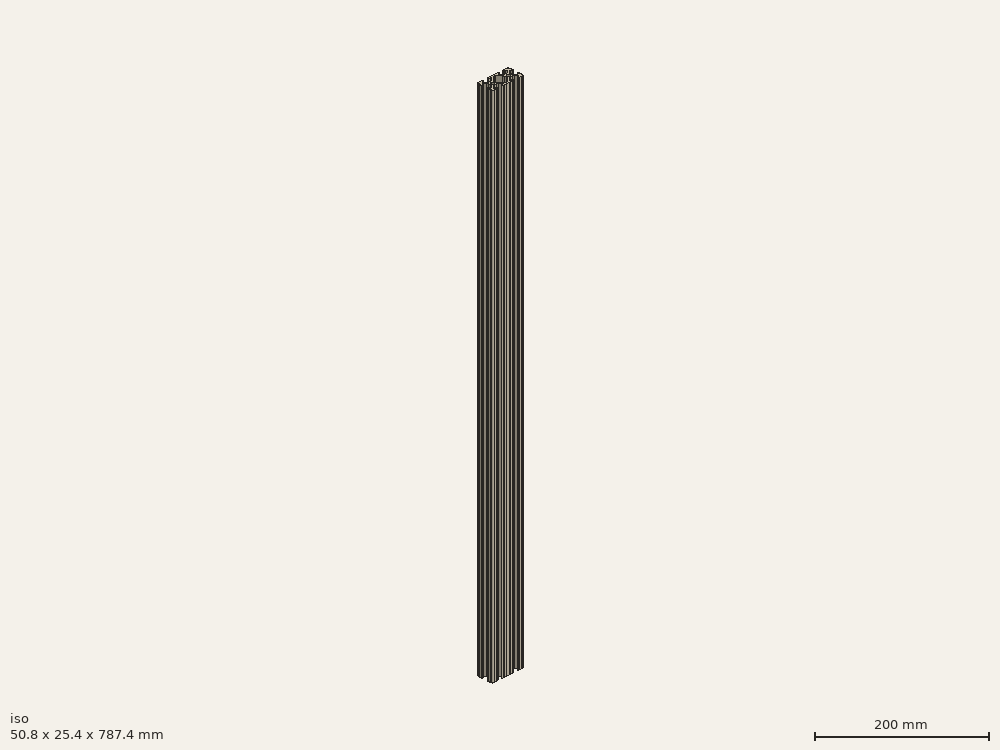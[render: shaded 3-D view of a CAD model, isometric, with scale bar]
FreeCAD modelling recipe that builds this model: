
FCSTD DOCUMENT  (FreeCAD 0.19R24267 (Git))
Label: 1020-31
License: All rights reserved
LicenseURL: http://en.wikipedia.org/wiki/All_rights_reserved
objects: Sketcher::SketchObject×1, Part::Extrusion×1
note: 2 computed .brp shape members not serialized (recipe doc carries the construction recipe); baked Part::Feature solids carry a one-line shape summary decoded from their .brp

FEATURE [Sketcher::SketchObject] Sketch162
  FullyConstrained = false
  sketch-geometry (162):
    g0: LineSegment StartX=7.25951 StartY=3.86941 StartZ=0 EndX=1.54575 EndY=9.57277 EndZ=0
    g1: LineSegment StartX=8.41248 StartY=-10.4902 StartZ=0 EndX=6.28364 EndY=-10.4902 EndZ=0
    g2: ArcOfCircle CenterX=8.41255 CenterY=-11.651 CenterZ=0 NormalX=0 NormalY=0 NormalZ=1 AngleXU=0 Radius=1.04895 StartAngle=4.71239 EndAngle=6.28319
    g3: LineSegment StartX=5.53258 StartY=-8.66607 StartZ=0 EndX=8.80999 EndY=-5.41626 EndZ=0
    g4: LineSegment StartX=9.4615 StartY=-11.651 StartZ=0 EndX=9.4615 EndY=-11.5392 EndZ=0
    g5: ArcOfCircle CenterX=8.41248 CenterY=-11.5392 CenterZ=0 NormalX=0 NormalY=0 NormalZ=1 AngleXU=0 Radius=1.04902 StartAngle=1.15714e-07 EndAngle=1.5708
    g6: ArcOfCircle CenterX=6.28364 CenterY=-9.42351 CenterZ=0 NormalX=0 NormalY=0 NormalZ=1 AngleXU=0 Radius=1.06669 StartAngle=2.35197 EndAngle=4.71239
    g7: LineSegment StartX=-7.28286 StartY=-3.84586 StartZ=0 EndX=-1.67557 EndY=-9.56109 EndZ=0
    g8: LineSegment StartX=1.50403 StartY=-9.57645 StartZ=0 EndX=7.25205 EndY=-3.87684 EndZ=0
    g9: LineSegment StartX=-0.551457 StartY=-10.033 StartZ=0 EndX=0.3952 EndY=-10.033 EndZ=0
    g10: LineSegment StartX=-1.54575 StartY=9.57277 StartZ=0 EndX=-7.25951 EndY=3.86941 EndZ=0
    g11: ArcOfCircle CenterX=0.3952 CenterY=-8.4582 CenterZ=0 NormalX=0 NormalY=0 NormalZ=1 AngleXU=0 Radius=1.5748 StartAngle=4.71239 EndAngle=5.49356
    g12: ArcOfCircle CenterX=5.0165 CenterY=-1.6223 CenterZ=0 NormalX=0 NormalY=0 NormalZ=1 AngleXU=0 Radius=3.175 StartAngle=5.49356 EndAngle=6.28319
    g13: LineSegment StartX=8.1915 StartY=-1.6223 StartZ=0 EndX=8.1915 EndY=1.6223 EndZ=0
    g14: LineSegment StartX=0.433213 StartY=10.033 StartZ=0 EndX=-0.433213 EndY=10.033 EndZ=0
    g15: ArcOfCircle CenterX=-0.551456 CenterY=-8.4582 CenterZ=0 NormalX=0 NormalY=0 NormalZ=1 AngleXU=0 Radius=1.5748 StartAngle=3.91746 EndAngle=4.71239
    g16: ArcOfCircle CenterX=-5.0165 CenterY=1.6223 CenterZ=0 NormalX=0 NormalY=0 NormalZ=1 AngleXU=0 Radius=3.175 StartAngle=2.35528 EndAngle=3.14159
    g17: ArcOfCircle CenterX=-0.433213 CenterY=8.4582 CenterZ=0 NormalX=0 NormalY=0 NormalZ=1 AngleXU=0 Radius=1.5748 StartAngle=1.5708 EndAngle=2.35528
    g18: ArcOfCircle CenterX=5.0165 CenterY=1.6223 CenterZ=0 NormalX=0 NormalY=0 NormalZ=1 AngleXU=0 Radius=3.175 StartAngle=2.15656e-07 EndAngle=0.78631
    g19: Circle CenterX=12.7 CenterY=-2.5e-15 CenterZ=0 NormalX=0 NormalY=0 NormalZ=-1 AngleXU=0 Radius=2.6035
    g20: Circle CenterX=-12.7 CenterY=2.5e-15 CenterZ=0 NormalX=0 NormalY=0 NormalZ=-1 AngleXU=0 Radius=2.6035
    g21: LineSegment StartX=-8.1915 StartY=1.6223 StartZ=0 EndX=-8.1915 EndY=-1.6223 EndZ=0
    g22: LineSegment StartX=-2.13358 StartY=-12.7 StartZ=0 EndX=2.13358 EndY=-12.7 EndZ=0
    g23: ArcOfCircle CenterX=-5.0165 CenterY=-1.6223 CenterZ=0 NormalX=0 NormalY=0 NormalZ=1 AngleXU=0 Radius=3.175 StartAngle=3.14159 EndAngle=3.91746
    g24: LineSegment StartX=3.14958 StartY=-12.7 StartZ=0 EndX=6.3669 EndY=-12.7 EndZ=0
    g25: ArcOfCircle CenterX=6.8749 CenterY=-12.7 CenterZ=0 NormalX=0 NormalY=0 NormalZ=1 AngleXU=0 Radius=0.508 StartAngle=0 EndAngle=3.14159
    g26: LineSegment StartX=-6.28939 StartY=-10.4902 StartZ=0 EndX=-8.41248 EndY=-10.4902 EndZ=0
    g27: LineSegment StartX=-8.41255 StartY=-12.7 StartZ=0 EndX=-7.38288 EndY=-12.7 EndZ=0
    g28: ArcOfCircle CenterX=0.433213 CenterY=8.4582 CenterZ=0 NormalX=0 NormalY=0 NormalZ=1 AngleXU=0 Radius=1.5748 StartAngle=0.78631 EndAngle=1.5708
    g29: ArcOfCircle CenterX=2.64158 CenterY=-12.7 CenterZ=0 NormalX=0 NormalY=0 NormalZ=1 AngleXU=0 Radius=0.508 StartAngle=0 EndAngle=3.14159
    g30: ArcOfCircle CenterX=-16.9875 CenterY=-11.5392 CenterZ=0 NormalX=0 NormalY=0 NormalZ=1 AngleXU=0 Radius=1.04902 StartAngle=1.16223e-07 EndAngle=1.5708
    g31: LineSegment StartX=-8.81696 StartY=-5.44724 StartZ=0 EndX=-5.56415 EndY=-8.76265 EndZ=0
    g32: LineSegment StartX=-16.9875 StartY=-10.4902 StartZ=0 EndX=-19.1164 EndY=-10.4902 EndZ=0
    g33: ArcOfCircle CenterX=-11.0833 CenterY=-7.6708 CenterZ=0 NormalX=0 NormalY=0 NormalZ=1 AngleXU=0 Radius=3.175 StartAngle=0.775866 EndAngle=1.5708
    g34: ArcOfCircle CenterX=-14.3449 CenterY=-7.6708 CenterZ=0 NormalX=0 NormalY=0 NormalZ=1 AngleXU=0 Radius=3.175 StartAngle=1.5708 EndAngle=2.3692
    g35: ArcOfCircle CenterX=-19.1164 CenterY=-9.4742 CenterZ=0 NormalX=0 NormalY=0 NormalZ=1 AngleXU=0 Radius=1.016 StartAngle=2.3692 EndAngle=4.71239
    g36: ArcOfCircle CenterX=-8.41248 CenterY=-11.5392 CenterZ=0 NormalX=0 NormalY=0 NormalZ=1 AngleXU=0 Radius=1.04902 StartAngle=1.5708 EndAngle=3.14159
    g37: LineSegment StartX=7.3829 StartY=-12.7 StartZ=0 EndX=8.41255 EndY=-12.7 EndZ=0
    g38: ArcOfCircle CenterX=-8.41255 CenterY=-11.651 CenterZ=0 NormalX=0 NormalY=0 NormalZ=1 AngleXU=0 Radius=1.04895 StartAngle=3.14159 EndAngle=4.71239
    g39: ArcOfCircle CenterX=14.3545 CenterY=-7.6708 CenterZ=0 NormalX=0 NormalY=0 NormalZ=1 AngleXU=0 Radius=3.175 StartAngle=0.789627 EndAngle=1.5708
    g40: ArcOfCircle CenterX=20.3835 CenterY=-1.55362 CenterZ=0 NormalX=0 NormalY=0 NormalZ=1 AngleXU=0 Radius=3.175 StartAngle=3.14159 EndAngle=3.93122
    g41: LineSegment StartX=23.1902 StartY=6.498 StartZ=0 EndX=23.1902 EndY=4.28752 EndZ=0
    g42: LineSegment StartX=-14.3449 StartY=-4.4958 StartZ=0 EndX=-11.0833 EndY=-4.4958 EndZ=0
    g43: LineSegment StartX=-19.8441 StartY=-8.76517 StartZ=0 EndX=-16.619 EndY=-5.45511 EndZ=0
    g44: LineSegment StartX=-6.36688 StartY=-12.7 StartZ=0 EndX=-3.14958 EndY=-12.7 EndZ=0
    g45: ArcOfCircle CenterX=-6.28939 CenterY=-9.4742 CenterZ=0 NormalX=0 NormalY=0 NormalZ=1 AngleXU=0 Radius=1.016 StartAngle=4.71239 EndAngle=7.05905
    g46: LineSegment StartX=-9.4615 StartY=-11.5392 StartZ=0 EndX=-9.4615 EndY=-11.6511 EndZ=0
    g47: ArcOfCircle CenterX=-6.87488 CenterY=-12.7 CenterZ=0 NormalX=0 NormalY=0 NormalZ=1 AngleXU=0 Radius=0.508 StartAngle=0 EndAngle=3.14159
    g48: LineSegment StartX=-15.9385 StartY=-11.651 StartZ=0 EndX=-15.9385 EndY=-11.5392 EndZ=0
    g49: ArcOfCircle CenterX=-2.64158 CenterY=-12.7 CenterZ=0 NormalX=0 NormalY=0 NormalZ=1 AngleXU=0 Radius=0.508 StartAngle=0 EndAngle=3.14159
    g50: ArcOfCircle CenterX=22.1596 CenterY=-6.33474 CenterZ=0 NormalX=0 NormalY=0 NormalZ=1 AngleXU=0 Radius=1.03057 StartAngle=3.93122 EndAngle=6.28319
    g51: ArcOfCircle CenterX=25.4 CenterY=5.82513 CenterZ=0 NormalX=0 NormalY=0 NormalZ=1 AngleXU=0 Radius=0.508 StartAngle=1.5708 EndAngle=4.71239
    g52: LineSegment StartX=25.4 StartY=6.33313 StartZ=0 EndX=25.4 EndY=9.5504 EndZ=0
    g53: LineSegment StartX=19.0331 StartY=-12.7 StartZ=0 EndX=22.2504 EndY=-12.7 EndZ=0
    g54: ArcOfCircle CenterX=20.3835 CenterY=1.69518 CenterZ=0 NormalX=0 NormalY=0 NormalZ=1 AngleXU=0 Radius=3.175 StartAngle=2.35528 EndAngle=3.14159
    g55: LineSegment StartX=16.9875 StartY=-12.7 StartZ=0 EndX=18.0171 EndY=-12.7 EndZ=0
    g56: ArcOfCircle CenterX=23.2918 CenterY=10.5918 CenterZ=0 NormalX=0 NormalY=0 NormalZ=1 AngleXU=0 Radius=2.1082 StartAngle=6.27114 EndAngle=7.86603
    g57: ArcOfCircle CenterX=24.2392 CenterY=-4.28752 CenterZ=0 NormalX=0 NormalY=0 NormalZ=1 AngleXU=0 Radius=1.04902 StartAngle=1.5708 EndAngle=3.14159
    g58: ArcOfCircle CenterX=24.401 CenterY=-4.23752 CenterZ=0 NormalX=0 NormalY=0 NormalZ=1 AngleXU=0 Radius=0.99902 StartAngle=1.41033e-07 EndAngle=1.5708
    g59: LineSegment StartX=16.59 StartY=-5.41626 StartZ=0 EndX=19.8674 EndY=-8.66607 EndZ=0
    g60: ArcOfCircle CenterX=16.9875 CenterY=-11.5392 CenterZ=0 NormalX=0 NormalY=0 NormalZ=1 AngleXU=0 Radius=1.04902 StartAngle=1.5708 EndAngle=3.14159
    g61: LineSegment StartX=22.2504 StartY=12.7 StartZ=0 EndX=19.0331 EndY=12.7 EndZ=0
    g62: ArcOfCircle CenterX=23.2918 CenterY=-10.5918 CenterZ=0 NormalX=0 NormalY=0 NormalZ=1 AngleXU=0 Radius=2.1082 StartAngle=4.70034 EndAngle=6.29523
    g63: ArcOfCircle CenterX=11.0455 CenterY=-7.6708 CenterZ=0 NormalX=0 NormalY=0 NormalZ=1 AngleXU=0 Radius=3.175 StartAngle=1.5708 EndAngle=2.35197
    g64: ArcOfCircle CenterX=22.7584 CenterY=12.7 CenterZ=0 NormalX=0 NormalY=0 NormalZ=1 AngleXU=0 Radius=0.508 StartAngle=3.14159 EndAngle=6.28288
    g65: LineSegment StartX=19.1164 StartY=-10.4902 StartZ=0 EndX=16.9875 EndY=-10.4902 EndZ=0
    g66: ArcOfCircle CenterX=22.7584 CenterY=-12.7 CenterZ=0 NormalX=0 NormalY=0 NormalZ=1 AngleXU=0 Radius=0.508 StartAngle=0.000301216 EndAngle=3.14159
    g67: ArcOfCircle CenterX=16.9875 CenterY=11.651 CenterZ=0 NormalX=0 NormalY=0 NormalZ=1 AngleXU=0 Radius=1.04902 StartAngle=1.5708 EndAngle=3.14159
    g68: ArcOfCircle CenterX=24.351 CenterY=4.28752 CenterZ=0 NormalX=0 NormalY=0 NormalZ=1 AngleXU=0 Radius=1.04902 StartAngle=4.71239 EndAngle=6.28319
    g69: ArcOfCircle CenterX=19.1164 CenterY=9.4742 CenterZ=0 NormalX=0 NormalY=0 NormalZ=1 AngleXU=0 Radius=1.016 StartAngle=5.49688 EndAngle=7.85398
    g70: LineSegment StartX=19.8341 StartY=8.75512 StartZ=0 EndX=16.4966 EndY=5.42369 EndZ=0
    g71: LineSegment StartX=18.0171 StartY=12.7 StartZ=0 EndX=16.9875 EndY=12.7 EndZ=0
    g72: ArcOfCircle CenterX=18.5251 CenterY=-12.7 CenterZ=0 NormalX=0 NormalY=0 NormalZ=1 AngleXU=0 Radius=0.508 StartAngle=0 EndAngle=3.14159
    g73: LineSegment StartX=15.9384 StartY=11.651 StartZ=0 EndX=15.9384 EndY=11.5392 EndZ=0
    g74: LineSegment StartX=16.9875 StartY=10.4902 StartZ=0 EndX=19.1164 EndY=10.4902 EndZ=0
    g75: LineSegment StartX=11.0455 StartY=-4.4958 StartZ=0 EndX=14.3545 EndY=-4.4958 EndZ=0
    g76: ArcOfCircle CenterX=14.2536 CenterY=7.6708 CenterZ=0 NormalX=0 NormalY=0 NormalZ=1 AngleXU=0 Radius=3.175 StartAngle=4.71239 EndAngle=5.49688
    g77: ArcOfCircle CenterX=25.4 CenterY=-5.82508 CenterZ=0 NormalX=0 NormalY=0 NormalZ=1 AngleXU=0 Radius=0.508 StartAngle=1.5708 EndAngle=4.71239
    g78: LineSegment StartX=18.1405 StartY=3.94229 StartZ=0 EndX=21.4316 EndY=7.22739 EndZ=0
    g79: LineSegment StartX=25.4 StartY=-5.31708 StartZ=0 EndX=25.4 EndY=-4.23752 EndZ=0
    g80: LineSegment StartX=14.2536 StartY=4.4958 StartZ=0 EndX=11.1464 EndY=4.4958 EndZ=0
    g81: ArcOfCircle CenterX=18.5251 CenterY=12.7 CenterZ=0 NormalX=0 NormalY=0 NormalZ=1 AngleXU=0 Radius=0.508 StartAngle=3.14159 EndAngle=6.28319
    g82: LineSegment StartX=23.1902 StartY=-4.28752 StartZ=0 EndX=23.1902 EndY=-6.33474 EndZ=0
    g83: LineSegment StartX=24.401 StartY=-3.2385 StartZ=0 EndX=24.2392 EndY=-3.2385 EndZ=0
    g84: ArcOfCircle CenterX=22.1596 CenterY=6.498 CenterZ=0 NormalX=0 NormalY=0 NormalZ=1 AngleXU=0 Radius=1.03057 StartAngle=0 EndAngle=2.35528
    g85: LineSegment StartX=15.9385 StartY=-11.5392 StartZ=0 EndX=15.9385 EndY=-11.6511 EndZ=0
    g86: LineSegment StartX=25.4 StartY=4.28752 StartZ=0 EndX=25.4 EndY=5.31713 EndZ=0
    g87: ArcOfCircle CenterX=11.1464 CenterY=7.6708 CenterZ=0 NormalX=0 NormalY=0 NormalZ=1 AngleXU=0 Radius=3.175 StartAngle=3.9279 EndAngle=4.71239
    g88: LineSegment StartX=8.90339 StartY=5.42369 StartZ=0 EndX=5.56588 EndY=8.75512 EndZ=0
    g89: LineSegment StartX=21.434 StartY=-7.06654 StartZ=0 EndX=18.148 EndY=-3.80816 EndZ=0
    g90: ArcOfCircle CenterX=25.4 CenterY=10.0584 CenterZ=0 NormalX=0 NormalY=0 NormalZ=1 AngleXU=0 Radius=0.508 StartAngle=1.5711 EndAngle=4.71239
    g91: ArcOfCircle CenterX=16.9875 CenterY=-11.651 CenterZ=0 NormalX=0 NormalY=0 NormalZ=1 AngleXU=0 Radius=1.04895 StartAngle=3.14159 EndAngle=4.71239
    g92: ArcOfCircle CenterX=19.1164 CenterY=-9.42352 CenterZ=0 NormalX=0 NormalY=0 NormalZ=1 AngleXU=0 Radius=1.06668 StartAngle=4.71239 EndAngle=7.07281
    g93: ArcOfCircle CenterX=24.2392 CenterY=4.28752 CenterZ=0 NormalX=0 NormalY=0 NormalZ=1 AngleXU=0 Radius=1.04902 StartAngle=3.14159 EndAngle=4.71239
    g94: ArcOfCircle CenterX=16.9875 CenterY=11.5392 CenterZ=0 NormalX=0 NormalY=0 NormalZ=1 AngleXU=0 Radius=1.04902 StartAngle=3.14159 EndAngle=4.71239
    g95: ArcOfCircle CenterX=25.4 CenterY=-10.0584 CenterZ=0 NormalX=0 NormalY=0 NormalZ=1 AngleXU=0 Radius=0.508 StartAngle=1.5708 EndAngle=4.71209
    g96: ArcOfCircle CenterX=6.87487 CenterY=12.7 CenterZ=0 NormalX=0 NormalY=0 NormalZ=1 AngleXU=0 Radius=0.508 StartAngle=3.14159 EndAngle=6.28319
    g97: LineSegment StartX=25.4 StartY=-9.5504 StartZ=0 EndX=25.4 EndY=-6.33308 EndZ=0
    g98: LineSegment StartX=17.2085 StartY=-1.55362 StartZ=0 EndX=17.2085 EndY=1.69518 EndZ=0
    g99: LineSegment StartX=-9.46155 StartY=11.651 StartZ=0 EndX=-9.46155 EndY=11.5392 EndZ=0
    g100: LineSegment StartX=24.2392 StartY=3.2385 StartZ=0 EndX=24.351 EndY=3.2385 EndZ=0
    g101: LineSegment StartX=-8.41253 StartY=10.4902 StartZ=0 EndX=-6.28939 EndY=10.4902 EndZ=0
    g102: ArcOfCircle CenterX=-10.8409 CenterY=7.6708 CenterZ=0 NormalX=0 NormalY=0 NormalZ=1 AngleXU=0 Radius=3.175 StartAngle=4.71239 EndAngle=5.49688
    g103: LineSegment StartX=-19.1164 StartY=10.4902 StartZ=0 EndX=-16.9875 EndY=10.4902 EndZ=0
    g104: LineSegment StartX=-10.8409 StartY=4.4958 StartZ=0 EndX=-14.1026 EndY=4.4958 EndZ=0
    g105: LineSegment StartX=-16.1879 StartY=5.27664 StartZ=0 EndX=-19.8682 EndY=8.48225 EndZ=0
    g106: LineSegment StartX=-7.38291 StartY=12.7 StartZ=0 EndX=-8.41253 EndY=12.7 EndZ=0
    g107: ArcOfCircle CenterX=-6.28939 CenterY=9.34546 CenterZ=0 NormalX=0 NormalY=0 NormalZ=1 AngleXU=0 Radius=1.14474 StartAngle=5.49688 EndAngle=7.85398
    g108: LineSegment StartX=6.28364 StartY=10.4902 StartZ=0 EndX=8.41253 EndY=10.4902 EndZ=0
    g109: ArcOfCircle CenterX=8.41253 CenterY=11.651 CenterZ=0 NormalX=0 NormalY=0 NormalZ=1 AngleXU=0 Radius=1.04902 StartAngle=4.29175e-07 EndAngle=1.5708
    g110: LineSegment StartX=9.46155 StartY=11.5392 StartZ=0 EndX=9.46155 EndY=11.651 EndZ=0
    g111: ArcOfCircle CenterX=-14.1026 CenterY=7.6708 CenterZ=0 NormalX=0 NormalY=0 NormalZ=1 AngleXU=0 Radius=3.175 StartAngle=3.99583 EndAngle=4.71239
    g112: LineSegment StartX=-5.48068 StartY=8.53527 StartZ=0 EndX=-8.59793 EndY=5.42369 EndZ=0
    g113: ArcOfCircle CenterX=-19.1164 CenterY=9.34546 CenterZ=0 NormalX=0 NormalY=0 NormalZ=1 AngleXU=0 Radius=1.14474 StartAngle=1.5708 EndAngle=3.99583
    g114: LineSegment StartX=8.41253 StartY=12.7 StartZ=0 EndX=7.38287 EndY=12.7 EndZ=0
    g115: LineSegment StartX=-3.14958 StartY=12.7 StartZ=0 EndX=-6.36691 EndY=12.7 EndZ=0
    g116: ArcOfCircle CenterX=-8.41253 CenterY=11.5392 CenterZ=0 NormalX=0 NormalY=0 NormalZ=1 AngleXU=0 Radius=1.04902 StartAngle=3.14159 EndAngle=4.71239
    g117: ArcOfCircle CenterX=8.41253 CenterY=11.5392 CenterZ=0 NormalX=0 NormalY=0 NormalZ=1 AngleXU=0 Radius=1.04902 StartAngle=4.71239 EndAngle=6.28319
    g118: ArcOfCircle CenterX=-6.87491 CenterY=12.7 CenterZ=0 NormalX=0 NormalY=0 NormalZ=1 AngleXU=0 Radius=0.508 StartAngle=3.14159 EndAngle=6.28319
    g119: ArcOfCircle CenterX=-8.41253 CenterY=11.651 CenterZ=0 NormalX=0 NormalY=0 NormalZ=1 AngleXU=0 Radius=1.04902 StartAngle=1.5708 EndAngle=3.14159
    g120: ArcOfCircle CenterX=-2.64159 CenterY=12.7 CenterZ=0 NormalX=0 NormalY=0 NormalZ=1 AngleXU=0 Radius=0.507987 StartAngle=3.14159 EndAngle=6.28319
    g121: ArcOfCircle CenterX=6.28364 CenterY=9.4742 CenterZ=0 NormalX=0 NormalY=0 NormalZ=1 AngleXU=0 Radius=1.016 StartAngle=1.5708 EndAngle=3.9279
    g122: LineSegment StartX=2.13361 StartY=12.7 StartZ=0 EndX=-2.13361 EndY=12.7 EndZ=0
    g123: LineSegment StartX=6.36687 StartY=12.7 StartZ=0 EndX=3.14961 EndY=12.7 EndZ=0
    g124: ArcOfCircle CenterX=-24.401 CenterY=4.23752 CenterZ=0 NormalX=0 NormalY=0 NormalZ=1 AngleXU=0 Radius=0.99902 StartAngle=3.14159 EndAngle=4.71239
    g125: LineSegment StartX=-16.9875 StartY=12.7 StartZ=0 EndX=-18.0171 EndY=12.7 EndZ=0
    g126: LineSegment StartX=-24.401 StartY=3.2385 StartZ=0 EndX=-24.1892 EndY=3.2385 EndZ=0
    g127: ArcOfCircle CenterX=2.64161 CenterY=12.7 CenterZ=0 NormalX=0 NormalY=0 NormalZ=1 AngleXU=0 Radius=0.508 StartAngle=3.14159 EndAngle=6.28319
    g128: ArcOfCircle CenterX=-22.2207 CenterY=-6.67687 CenterZ=0 NormalX=0 NormalY=0 NormalZ=1 AngleXU=0 Radius=0.969476 StartAngle=3.14159 EndAngle=5.51079
    g129: LineSegment StartX=-18.1094 StartY=-3.8465 StartZ=0 EndX=-21.5263 EndY=-7.35342 EndZ=0
    g130: LineSegment StartX=-17.2085 StartY=1.63081 StartZ=0 EndX=-17.2085 EndY=-1.63081 EndZ=0
    g131: ArcOfCircle CenterX=-22.2207 CenterY=6.15588 CenterZ=0 NormalX=0 NormalY=0 NormalZ=1 AngleXU=0 Radius=0.969476 StartAngle=0.854233 EndAngle=3.14159
    g132: LineSegment StartX=-24.1892 StartY=-3.2385 StartZ=0 EndX=-24.401 EndY=-3.2385 EndZ=0
    g133: ArcOfCircle CenterX=-25.4 CenterY=10.0584 CenterZ=0 NormalX=0 NormalY=0 NormalZ=1 AngleXU=0 Radius=0.508 StartAngle=4.71239 EndAngle=7.85368
    g134: LineSegment StartX=-23.1902 StartY=-6.67687 StartZ=0 EndX=-23.1902 EndY=-4.23752 EndZ=0
    g135: ArcOfCircle CenterX=-20.3835 CenterY=-1.63081 CenterZ=0 NormalX=0 NormalY=0 NormalZ=1 AngleXU=0 Radius=3.175 StartAngle=5.51079 EndAngle=6.28319
    g136: ArcOfCircle CenterX=-24.1892 CenterY=-4.23752 CenterZ=0 NormalX=0 NormalY=0 NormalZ=1 AngleXU=0 Radius=0.99902 StartAngle=1.41033e-07 EndAngle=1.5708
    g137: ArcOfCircle CenterX=-25.4 CenterY=5.82508 CenterZ=0 NormalX=0 NormalY=0 NormalZ=1 AngleXU=0 Radius=0.508 StartAngle=4.71239 EndAngle=7.85398
    g138: LineSegment StartX=-23.1902 StartY=4.23752 StartZ=0 EndX=-23.1902 EndY=6.15588 EndZ=0
    g139: LineSegment StartX=-15.9384 StartY=11.5392 StartZ=0 EndX=-15.9384 EndY=11.651 EndZ=0
    g140: ArcOfCircle CenterX=-22.7584 CenterY=12.7 CenterZ=0 NormalX=0 NormalY=0 NormalZ=1 AngleXU=0 Radius=0.508 StartAngle=3.14189 EndAngle=6.28319
    g141: LineSegment StartX=-19.0331 StartY=12.7 StartZ=0 EndX=-22.2504 EndY=12.7 EndZ=0
    g142: ArcOfCircle CenterX=-16.9875 CenterY=11.651 CenterZ=0 NormalX=0 NormalY=0 NormalZ=1 AngleXU=0 Radius=1.04902 StartAngle=4.28571e-07 EndAngle=1.5708
    g143: ArcOfCircle CenterX=-18.5251 CenterY=12.7 CenterZ=0 NormalX=0 NormalY=0 NormalZ=1 AngleXU=0 Radius=0.508 StartAngle=3.14159 EndAngle=6.28319
    g144: ArcOfCircle CenterX=-24.1892 CenterY=4.23752 CenterZ=0 NormalX=0 NormalY=0 NormalZ=1 AngleXU=0 Radius=0.99902 StartAngle=4.71239 EndAngle=6.28319
    g145: LineSegment StartX=-25.4 StartY=5.31708 StartZ=0 EndX=-25.4 EndY=4.23752 EndZ=0
    g146: ArcOfCircle CenterX=-16.9875 CenterY=11.5392 CenterZ=0 NormalX=0 NormalY=0 NormalZ=1 AngleXU=0 Radius=1.04902 StartAngle=4.71239 EndAngle=6.28319
    g147: LineSegment StartX=-21.584 StartY=6.88693 StartZ=0 EndX=-18.2982 EndY=4.02497 EndZ=0
    g148: ArcOfCircle CenterX=-20.3835 CenterY=1.63081 CenterZ=0 NormalX=0 NormalY=0 NormalZ=1 AngleXU=0 Radius=3.175 StartAngle=0 EndAngle=0.854233
    g149: ArcOfCircle CenterX=-23.2918 CenterY=10.5918 CenterZ=0 NormalX=0 NormalY=0 NormalZ=1 AngleXU=0 Radius=2.1082 StartAngle=1.55875 EndAngle=3.15364
    g150: LineSegment StartX=-25.4 StartY=9.5504 StartZ=0 EndX=-25.4 EndY=6.33308 EndZ=0
    g151: LineSegment StartX=-25.4 StartY=-4.23752 StartZ=0 EndX=-25.4 EndY=-5.31708 EndZ=0
    g152: ArcOfCircle CenterX=-23.2918 CenterY=-10.5918 CenterZ=0 NormalX=0 NormalY=0 NormalZ=1 AngleXU=0 Radius=2.1082 StartAngle=3.12954 EndAngle=4.72444
    g153: ArcOfCircle CenterX=-22.7584 CenterY=-12.7 CenterZ=0 NormalX=0 NormalY=0 NormalZ=1 AngleXU=0 Radius=0.508 StartAngle=0 EndAngle=3.14129
    g154: LineSegment StartX=-18.0171 StartY=-12.7 StartZ=0 EndX=-16.9875 EndY=-12.7 EndZ=0
    g155: ArcOfCircle CenterX=-25.4 CenterY=-10.0584 CenterZ=0 NormalX=0 NormalY=0 NormalZ=1 AngleXU=0 Radius=0.508 StartAngle=4.71269 EndAngle=7.85398
    g156: LineSegment StartX=-22.2504 StartY=-12.7 StartZ=0 EndX=-19.0331 EndY=-12.7 EndZ=0
    g157: ArcOfCircle CenterX=-16.9875 CenterY=-11.651 CenterZ=0 NormalX=0 NormalY=0 NormalZ=1 AngleXU=0 Radius=1.04895 StartAngle=4.71239 EndAngle=6.28319
    g158: ArcOfCircle CenterX=-24.401 CenterY=-4.23752 CenterZ=0 NormalX=0 NormalY=0 NormalZ=1 AngleXU=0 Radius=0.99902 StartAngle=1.5708 EndAngle=3.14159
    g159: ArcOfCircle CenterX=-25.4 CenterY=-5.82513 CenterZ=0 NormalX=0 NormalY=0 NormalZ=1 AngleXU=0 Radius=0.508051 StartAngle=4.71239 EndAngle=7.85398
    g160: ArcOfCircle CenterX=-18.5251 CenterY=-12.7 CenterZ=0 NormalX=0 NormalY=0 NormalZ=1 AngleXU=0 Radius=0.508 StartAngle=0 EndAngle=3.14159
    g161: LineSegment StartX=-25.4 StartY=-6.33319 StartZ=0 EndX=-25.4 EndY=-9.5504 EndZ=0
  constraints (160):
    c: Coincident(g161,g155)
    c: Coincident(g159,g161)
    c: Coincident(g151,g159)
    c: Coincident(g158,g151)
    c: Coincident(g124,g145)
    c: Coincident(g137,g145)
    c: Coincident(g137,g150)
    c: Coincident(g133,g150)
    c: Coincident(g152,g155)
    c: Coincident(g149,g133)
    c: Coincident(g158,g132)
    c: Coincident(g124,g126)
    c: Coincident(g136,g132)
    c: Coincident(g144,g126)
    c: Coincident(g153,g152)
    c: Coincident(g140,g149)
    c: Coincident(g134,g128)
    c: Coincident(g134,g136)
    c: Coincident(g138,g144)
    c: Coincident(g131,g138)
    c: Coincident(g153,g156)
    c: Coincident(g141,g140)
    c: Coincident(g131,g147)
    c: Coincident(g129,g128)
    c: Coincident(g105,g113)
    c: Coincident(g35,g43)
    c: Coincident(g35,g32)
    c: Coincident(g113,g103)
    c: Coincident(g156,g160)
    c: Coincident(g143,g141)
    c: Coincident(g147,g148)
    c: Coincident(g135,g129)
    c: Coincident(g154,g160)
    c: Coincident(g143,g125)
    c: Coincident(g130,g135)
    c: Coincident(g130,g148)
    c: Coincident(g154,g157)
    c: Coincident(g32,g30)
    c: Coincident(g103,g146)
    c: Coincident(g142,g125)
    c: Coincident(g43,g34)
    c: Coincident(g111,g105)
    c: Coincident(g157,g48)
    c: Coincident(g48,g30)
    c: Coincident(g139,g146)
    c: Coincident(g139,g142)
    c: Coincident(g42,g34)
    c: Coincident(g104,g111)
    c: Coincident(g33,g42)
    c: Coincident(g102,g104)
    c: Coincident(g38,g46)
    c: Coincident(g46,g36)
    c: Coincident(g99,g116)
    c: Coincident(g119,g99)
    c: Coincident(g33,g31)
    c: Coincident(g102,g112)
    c: Coincident(g27,g38)
    c: Coincident(g36,g26)
    c: Coincident(g116,g101)
    c: Coincident(g106,g119)
    c: Coincident(g21,g23)
    c: Coincident(g21,g16)
    c: Coincident(g27,g47)
    c: Coincident(g106,g118)
    c: Coincident(g23,g7)
    c: Coincident(g10,g16)
    c: Coincident(g44,g47)
    c: Coincident(g118,g115)
    c: Coincident(g45,g26)
    c: Coincident(g107,g101)
    c: Coincident(g45,g31)
    c: Coincident(g112,g107)
    c: Coincident(g44,g49)
    c: Coincident(g120,g115)
    c: Coincident(g22,g49)
    c: Coincident(g122,g120)
    c: Coincident(g15,g7)
    c: Coincident(g10,g17)
    c: Coincident(g9,g15)
    c: Coincident(g17,g14)
    c: Coincident(g9,g11)
    c: Coincident(g14,g28)
    c: Coincident(g8,g11)
    c: Coincident(g0,g28)
    c: Coincident(g29,g22)
    c: Coincident(g122,g127)
    c: Coincident(g24,g29)
    c: Coincident(g123,g127)
    c: Coincident(g3,g6)
    c: Coincident(g88,g121)
    c: Coincident(g1,g6)
    c: Coincident(g108,g121)
    c: Coincident(g25,g24)
    c: Coincident(g96,g123)
    c: Coincident(g8,g12)
    c: Coincident(g18,g0)
    c: Coincident(g25,g37)
    c: Coincident(g96,g114)
    c: Coincident(g12,g13)
    c: Coincident(g18,g13)
    c: Coincident(g2,g37)
    c: Coincident(g5,g1)
    c: Coincident(g117,g108)
    c: Coincident(g109,g114)
    c: Coincident(g3,g63)
    c: Coincident(g87,g88)
    c: Coincident(g2,g4)
    c: Coincident(g5,g4)
    c: Coincident(g117,g110)
    c: Coincident(g109,g110)
    c: Coincident(g75,g63)
    c: Coincident(g80,g87)
    c: Coincident(g80,g76)
    c: Coincident(g39,g75)
    c: Coincident(g85,g91)
    c: Coincident(g85,g60)
    c: Coincident(g73,g94)
    c: Coincident(g73,g67)
    c: Coincident(g70,g76)
    c: Coincident(g59,g39)
    c: Coincident(g55,g91)
    c: Coincident(g60,g65)
    c: Coincident(g94,g74)
    c: Coincident(g67,g71)
    c: Coincident(g40,g98)
    c: Coincident(g54,g98)
    c: Coincident(g55,g72)
    c: Coincident(g71,g81)
    c: Coincident(g78,g54)
    c: Coincident(g40,g89)
    c: Coincident(g53,g72)
    c: Coincident(g61,g81)
    c: Coincident(g65,g92)
    c: Coincident(g74,g69)
    c: Coincident(g70,g69)
    c: Coincident(g59,g92)
    c: Coincident(g84,g78)
    c: Coincident(g50,g89)
    c: Coincident(g53,g66)
    c: Coincident(g64,g61)
    c: Coincident(g82,g50)
    c: Coincident(g57,g82)
    c: Coincident(g41,g93)
    c: Coincident(g41,g84)
    c: Coincident(g62,g66)
    c: Coincident(g64,g56)
    c: Coincident(g57,g83)
    c: Coincident(g100,g93)
    c: Coincident(g100,g68)
    c: Coincident(g58,g83)
    c: Coincident(g62,g95)
    c: Coincident(g56,g90)
    c: Coincident(g97,g95)
    c: Coincident(g97,g77)
    c: Coincident(g77,g79)
    c: Coincident(g58,g79)
    c: Coincident(g68,g86)
    c: Coincident(g86,g51)
    c: Coincident(g51,g52)
    c: Coincident(g52,g90)
FEATURE [Part::Extrusion] Extrude
  Base = -> Sketch162
  Dir = (0,0,1)
  DirMode = 2
  FaceMakerClass = Part::FaceMakerBullseye
  LengthFwd = 787.4
  LengthRev = 0
  Solid = true
  Symmetric = false
